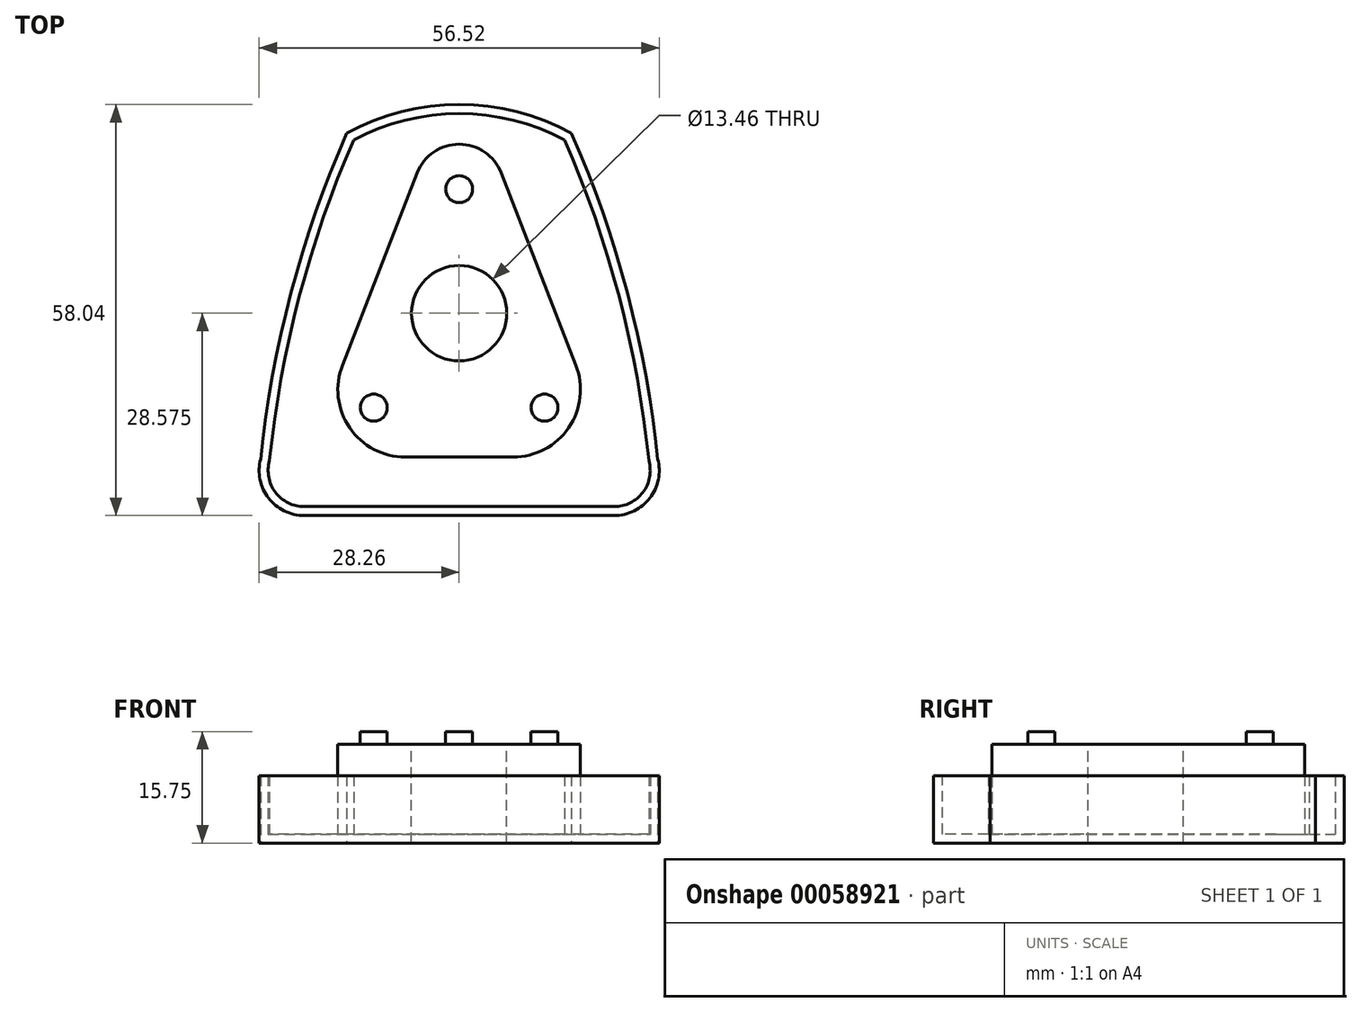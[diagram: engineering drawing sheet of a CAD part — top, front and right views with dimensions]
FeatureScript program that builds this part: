
annotation { "Feature Type Name" : "Feature", "Feature Type Description" : "" }
export const myFeature = defineFeature(function(context is Context, id is Id, definition is map)
    precondition{}
    {
        {
            var Q0;
            Q0=qCreatedBy(makeId("Top.planeOp"),FACE);
            var sketch = newSketch(context, id + "F0", { "sketchPlane" : qUnion([Q0])});
            skLineSegment(sketch, "E0", {"start": v(-21.91, 0) * mm, "end": v(21.91, 0) * mm});
            skPoint(sketch, "E1.visualSharp", {"position": v(-30.16, 0) * mm});
            skArc(sketch, "E1.filletArc", {"start": v(-28.05, 7.97) * mm, "mid": v(-26.94, 2.48) * mm, "end": v(-21.91, 0) * mm});
            skPoint(sketch, "E2.visualSharp", {"position": v(30.16, 0) * mm});
            skArc(sketch, "E2.filletArc", {"start": v(21.91, 0) * mm, "mid": v(26.94, 2.48) * mm, "end": v(28.05, 7.97) * mm});
            skArc(sketch, "E3", {"start": v(-15.88, 53.98) * mm, "mid": v(-23.77, 31.45) * mm, "end": v(-28.05, 7.97) * mm});
            skArc(sketch, "E4", {"start": v(28.05, 7.97) * mm, "mid": v(23.77, 31.45) * mm, "end": v(15.88, 53.98) * mm});
            skArc(sketch, "E5", {"start": v(15.87, 53.98) * mm, "mid": v(0, 58.04) * mm, "end": v(-15.87, 53.98) * mm});
            skSolve(sketch);
        }
        {
            var Q0;
            Q0=makeQuery(id+"F0.imprint","IMPRINT",FACE,{"disambiguationData":[TD([[makeQuery(id+"F0.imprint","IMPRINT",EDGE,{"derivedFrom":sQuery(id+"F0.wireOp",EDGE,"E0")}),1.0]])]});
            extrude(context, id + "F1", {"entities" : qUnion([Q0]), "depth" : 9.52 * mm});
        }
        {
            var Q0;
            Q0=makeQuery(id+"F1.opExtrude","CAP_FACE",FACE,{"disambiguationData":[OSD([sQuery(id+"F0.wireOp",EDGE,"E0"),sQuery(id+"F0.wireOp",EDGE,"E1.filletArc"),sQuery(id+"F0.wireOp",EDGE,"E2.filletArc"),sQuery(id+"F0.wireOp",EDGE,"E3"),sQuery(id+"F0.wireOp",EDGE,"E4"),sQuery(id+"F0.wireOp",EDGE,"E5")])],"isStart":false});
            shell(context, id + "F2", {"entities" : qUnion([Q0]), "thickness" : 1.27 * mm});
        }
        {
            var Q0;
            Q0=makeQuery(id+"F2.opShell","OFFSET_FACE",FACE,{"disambiguationData":[OSD([sQuery(id+"F0.wireOp",EDGE,"E0"),sQuery(id+"F0.wireOp",EDGE,"E1.filletArc"),sQuery(id+"F0.wireOp",EDGE,"E2.filletArc"),sQuery(id+"F0.wireOp",EDGE,"E3"),sQuery(id+"F0.wireOp",EDGE,"E4"),sQuery(id+"F0.wireOp",EDGE,"E5")])]});
            var sketch = newSketch(context, id + "F3", { "sketchPlane" : qUnion([Q0])});
            skArc(sketch, "E6", {"start": v(5.92, 48.4) * mm, "mid": v(0, 52.45) * mm, "end": v(-5.92, 48.4) * mm});
            skArc(sketch, "E7", {"start": v(7.62, 8.26) * mm, "mid": v(15.64, 12.64) * mm, "end": v(16.27, 21.76) * mm});
            skArc(sketch, "E8", {"start": v(-16.27, 21.76) * mm, "mid": v(-15.64, 12.64) * mm, "end": v(-7.62, 8.26) * mm});
            skLineSegment(sketch, "E9", {"start": v(-7.62, 8.25) * mm, "end": v(7.62, 8.25) * mm});
            skLineSegment(sketch, "E10", {"start": v(5.92, 48.4) * mm, "end": v(16.5, 21.24) * mm});
            skLineSegment(sketch, "E11", {"start": v(-5.92, 48.4) * mm, "end": v(-16.64, 20.86) * mm});
            skPoint(sketch, "E12", {"position": v(-16.27, 21.76) * mm});
            skPoint(sketch, "E13", {"position": v(16.27, 21.76) * mm});
            skPoint(sketch, "E14", {"position": v(0, 52.45) * mm});
            skSolve(sketch);
        }
        {
            var Q0;
            {var subQ6=sQuery(id+"F3.wireOp",EDGE,"E6");Q0=makeQuery(id+"F3.imprint","IMPRINT",FACE,{"disambiguationData":[TD([[makeQuery(id+"F3.imprint","IMPRINT",EDGE,{"derivedFrom":subQ6}),1.0]])]});}
            extrude(context, id + "F4", {"entities" : qUnion([Q0]), "operationType" : NewBodyOperationType.ADD, "depth" : 12.7 * mm});
        }
        {
            var Q0;
            Q0=makeQuery(id+"F4.opExtrude","CAP_FACE",FACE,{"disambiguationData":[OSD([sQuery(id+"F3.wireOp",EDGE,"E6"),sQuery(id+"F3.wireOp",EDGE,"E7"),sQuery(id+"F3.wireOp",EDGE,"E8"),sQuery(id+"F3.wireOp",EDGE,"E9"),sQuery(id+"F3.wireOp",EDGE,"E10"),sQuery(id+"F3.wireOp",EDGE,"E11")])],"isStart":false});
            var sketch = newSketch(context, id + "F5", { "sketchPlane" : qUnion([Q0])});
            skCircle(sketch, "E15", {"center": v(0, 46.1) * mm, "radius": 1.9 * mm});
            skCircle(sketch, "E16", {"center": v(12.07, 15.24) * mm, "radius": 1.9 * mm});
            skCircle(sketch, "E17", {"center": v(-12.07, 15.24) * mm, "radius": 1.9 * mm});
            skCircle(sketch, "E18", {"center": v(0, 28.58) * mm, "radius": 6.73 * mm});
            skSolve(sketch);
        }
        {
            var Q0;
            Q0=makeQuery(id+"F5.imprint","IMPRINT",FACE,{"disambiguationData":[TD([[makeQuery(id+"F5.imprint","IMPRINT",EDGE,{"derivedFrom":sQuery(id+"F5.wireOp",EDGE,"E15")}),1.0]])]});
            var Q1;
            Q1=makeQuery(id+"F5.imprint","IMPRINT",FACE,{"disambiguationData":[TD([[makeQuery(id+"F5.imprint","IMPRINT",EDGE,{"derivedFrom":sQuery(id+"F5.wireOp",EDGE,"E17")}),1.0]])]});
            var Q2;
            Q2=makeQuery(id+"F5.imprint","IMPRINT",FACE,{"disambiguationData":[TD([[makeQuery(id+"F5.imprint","IMPRINT",EDGE,{"derivedFrom":sQuery(id+"F5.wireOp",EDGE,"E16")}),1.0]])]});
            extrude(context, id + "F6", {"entities" : qUnion([Q0, Q1, Q2]), "operationType" : NewBodyOperationType.ADD, "depth" : 1.78 * mm});
        }
        {
            var Q0;
            Q0=makeQuery(id+"F5.imprint","IMPRINT",FACE,{"disambiguationData":[TD([[makeQuery(id+"F5.imprint","IMPRINT",EDGE,{"derivedFrom":sQuery(id+"F5.wireOp",EDGE,"E18")}),1.0]])]});
            extrude(context, id + "F7", {"entities" : qUnion([Q0]), "operationType" : NewBodyOperationType.REMOVE, "endBound" : BoundingType.THROUGH_ALL, "oppositeDirection" : true, "depth" : 6.35 * mm});
        }
    });
